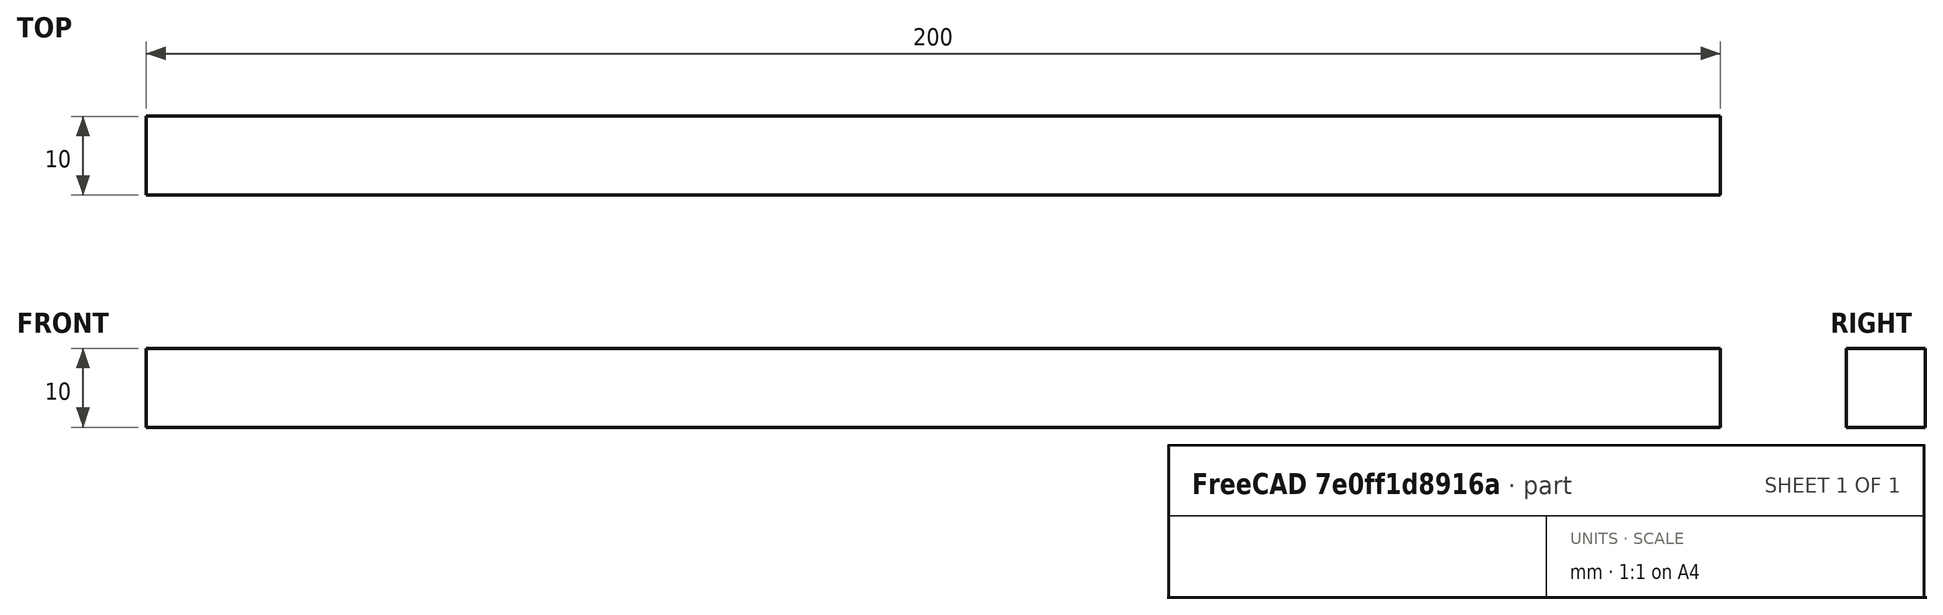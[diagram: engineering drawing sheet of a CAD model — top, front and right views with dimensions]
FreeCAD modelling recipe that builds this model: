
FCSTD DOCUMENT  (FreeCAD 0.18R4 (GitTag))
Label: Bar-B
License: All rights reserved
LicenseURL: http://en.wikipedia.org/wiki/All_rights_reserved
objects: Sketcher::SketchObject×1, PartDesign::Pad×1, PartDesign::Body×1
note: 4 computed .brp shape members not serialized (recipe doc carries the construction recipe); baked Part::Feature solids carry a one-line shape summary decoded from their .brp

FEATURE [Sketcher::SketchObject] Sketch
  MapMode = 5
  Placement = pos=(0,0,0) rot=(0.57735,0.57735,0.57735;2.0944rad)
  Support = -> [YZ_Plane]
  sketch-geometry (4):
    g0: LineSegment StartX=-0.0850123 StartY=0.0884153 StartZ=0 EndX=-10.085 EndY=0.0884153 EndZ=0
    g1: LineSegment StartX=-10.085 StartY=0.0884153 StartZ=0 EndX=-10.085 EndY=10.0884 EndZ=0
    g2: LineSegment StartX=-10.085 StartY=10.0884 StartZ=0 EndX=-0.0850123 EndY=10.0884 EndZ=0
    g3: LineSegment StartX=-0.0850123 StartY=10.0884 StartZ=0 EndX=-0.0850123 EndY=0.0884153 EndZ=0
  constraints (10):
    c: Coincident(g0,g1)
    c: Coincident(g1,g2)
    c: Coincident(g2,g3)
    c: Coincident(g3,g0)
    c: Horizontal(g0)
    c: Horizontal(g2)
    c: Vertical(g1)
    c: Vertical(g3)
    c: Distance(g3) = 10
    c: Distance(g2) = 10
FEATURE [PartDesign::Pad] Pad
  Length = 200
  Length2 = 100
  Placement = pos=(0,0,0) rot=(0.57735,0.57735,0.57735;2.0944rad)
  Profile = -> Sketch
  Type = 0
FEATURE [PartDesign::Body] Body
  Group = -> [Sketch,Pad]
  Origin = -> Origin
  Tip = -> Pad
